# Revit family: ES 3.RFA
name_source: partatom
category: Generic Models
revit_build: Autodesk Revit MEP 2013 (Build: 20130531_2115(x64)
units: mm (PartAtom-declared; Revit-internal decimal feet)

## types (1)
- ES 3  Electronic Instantaneous Water Heater
    BMS Links = No
    Backflow Prevention Valve = Not Supplied
    Button Interface = No
    Cable Length and size (If Fitted) = Not Fitted
    Control Thermostat Range = 30°C-43°C
    Enclosure Rating = IP25
    External Material = High Impact
    Factory set flow rate ES_ - @3 bar l/m = 2.0
    Factory set flow rate ES_3 - @3 bar l/m = 2.5
    Factory set flow rate ES_4 - @3 bar l/m = 3.3
    Gross Weight = 1.5kg
    Internal Filter (if fitted) = No
    Mains Pressure Limiting Valve = Not Supplied
    Mains Water Connection = 1/2" BSP
    Mains Water Pressure _ Minimum = A minimum water pressure of 0.2 MPa (2 bar) is recommended for optimum performance.
    Manufacturer = Zip Industries(UK) Ltd
    Model = ES3
    Net Weight = 1.3kg
    Overall Height = 135mm
    Overall Length/Depth = 87mm
    Overall Width = 186mm
    Power Rating ES_3 = 2.8kW
    Power Supply (Voltage) = 230 (v~)
    Product Range = Instantaneous
    Programmable Function Parameters = No
    Programmable Safety Features = No
    Shape = Rectangular
    Shipping Weight = Not Known
    Standby Power Loss (idle mode) = Not Known
    Supply Phase = 1
    Type = Wall mounted instantaneous water heater
    Type Comments = Wall Mounted Water Heater
    URL = www.zipindustries.co.uk
    WRAS Approved = Yes
    Warranty ID = 12 Calender Months
    Wireless (WIFI) = No

## geometry (parser evidence)
native form markers: Sweep x3
no freeform markers — native parametric forms only
